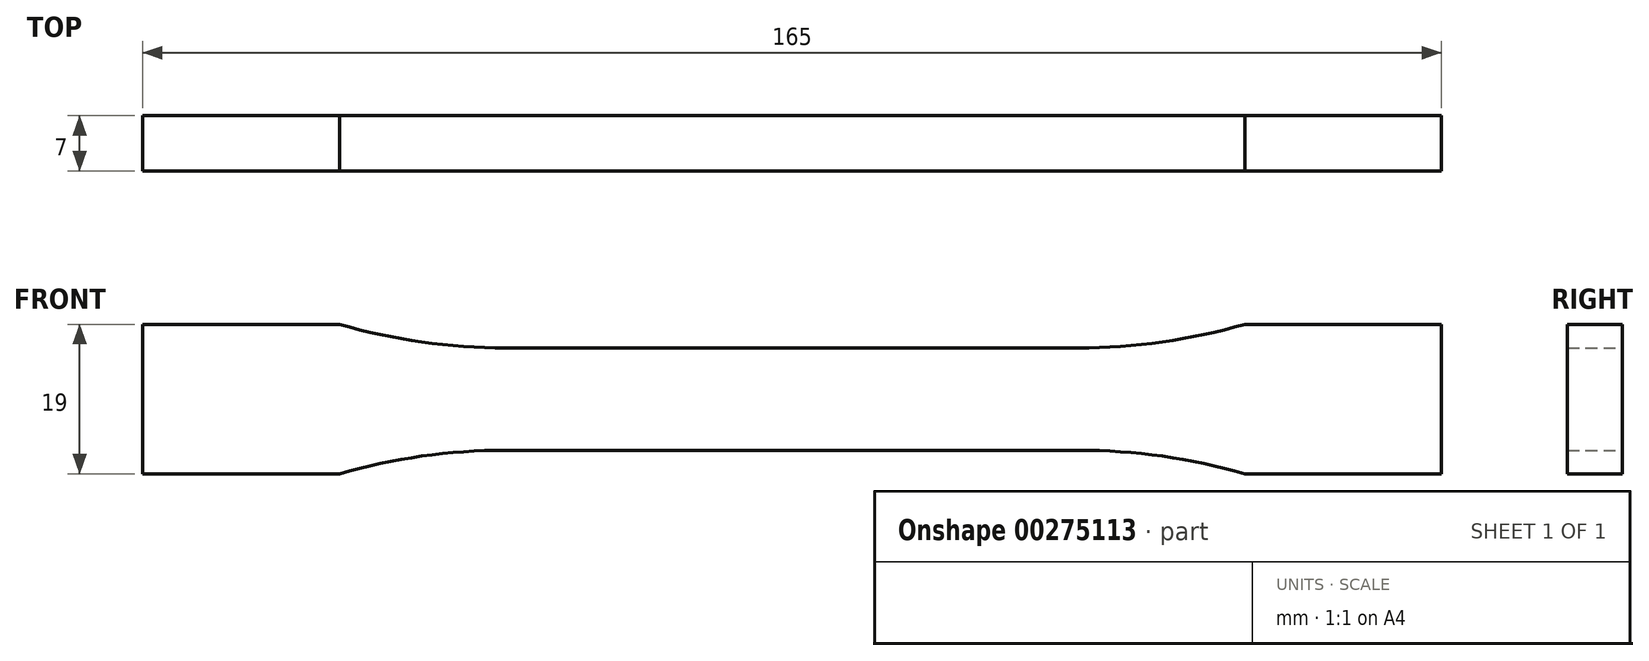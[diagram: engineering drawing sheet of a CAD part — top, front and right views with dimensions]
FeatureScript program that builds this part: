
annotation { "Feature Type Name" : "Feature", "Feature Type Description" : "" }
export const myFeature = defineFeature(function(context is Context, id is Id, definition is map)
    precondition{}
    {
        {
            var Q0;
            Q0=qCreatedBy(makeId("Front.planeOp"),FACE);
            var sketch = newSketch(context, id + "F0", { "sketchPlane" : qUnion([Q0])});
            skLineSegment(sketch, "E0", {"start": v(0, 6.5) * mm, "end": v(36.36, 6.5) * mm});
            skArc(sketch, "E1", {"start": v(36.36, 6.5) * mm, "mid": v(47.03, 7.25) * mm, "end": v(57.5, 9.5) * mm});
            skLineSegment(sketch, "E2", {"start": v(57.5, 9.5) * mm, "end": v(82.5, 9.5) * mm});
            skArc(sketch, "E3.MirrorCS", {"start": v(36.36, -6.5) * mm, "mid": v(47.03, -7.25) * mm, "end": v(57.5, -9.5) * mm});
            skLineSegment(sketch, "E4.MirrorCS", {"start": v(0, -6.5) * mm, "end": v(36.36, -6.5) * mm});
            skLineSegment(sketch, "E5.MirrorCS", {"start": v(57.5, -9.5) * mm, "end": v(82.5, -9.5) * mm});
            skLineSegment(sketch, "E6.MirrorCS", {"start": v(0, -6.5) * mm, "end": v(-36.36, -6.5) * mm});
            skLineSegment(sketch, "E7.MirrorCS", {"start": v(-57.5, 9.5) * mm, "end": v(-82.5, 9.5) * mm});
            skArc(sketch, "E8.MirrorCS", {"start": v(-36.36, -6.5) * mm, "mid": v(-47.03, -7.25) * mm, "end": v(-57.5, -9.5) * mm});
            skLineSegment(sketch, "E9.MirrorCS", {"start": v(0, 6.5) * mm, "end": v(-36.36, 6.5) * mm});
            skLineSegment(sketch, "E10.MirrorCS", {"start": v(-57.5, -9.5) * mm, "end": v(-82.5, -9.5) * mm});
            skArc(sketch, "E11.MirrorCS", {"start": v(-36.36, 6.5) * mm, "mid": v(-47.03, 7.25) * mm, "end": v(-57.5, 9.5) * mm});
            skLineSegment(sketch, "E12", {"start": v(-82.5, 9.5) * mm, "end": v(-82.5, -9.5) * mm});
            skLineSegment(sketch, "E13", {"start": v(82.5, 9.5) * mm, "end": v(82.5, -9.5) * mm});
            skSolve(sketch);
        }
        {
            var Q0;
            Q0 = qSketchRegion(id + "F0", true);
            extrude(context, id + "F1", {"entities" : qUnion([Q0]), "endBound" : BoundingType.SYMMETRIC, "depth" : 7 * mm});
        }
    });
